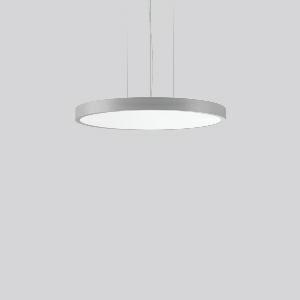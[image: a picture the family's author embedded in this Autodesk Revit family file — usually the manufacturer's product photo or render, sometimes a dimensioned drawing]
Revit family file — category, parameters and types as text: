
# Revit family: triona_round_p_312386_004_1_76_df9a
name_source: partatom
category: Lighting Fixtures
units: mm (PartAtom-declared; Revit-internal decimal feet)

## family parameters
Cut with Voids When Loaded = No
Host = Face
Light Source = No
Part Type = Normal
Room Calculation Point = No
Round Connector Dimension = Use Diameter
Shared = No

## types (1)
- TRIONA round P (1 x LED Modul 840, 9650 lm, 4000)
    Apparent Load = 106 VA
    CIE Flux Codes = 49 80 96 72 100
    Color Rendering = 80
    Color Temperature = 4000
    Default Elevation = 1800 mm
    Description = Series: TRIONA round
Decorative round LED pendant-mounted surface luminaire. Flat, seamless frame: aluminium extrusion profile, powder coated. Cover made of sheet steel, powder-coated. Canopy made of aluminium, powder-coated. Direct light emission through a diffuser plastic opal. Indirect light emission through a flush diffuser made of satin-finish plastic. Lightguide and diffuser made of non-yellowing plastic (PMMA). Lateral light emission (RZB SIDELITE technology) for above-average homogeneous light distribution. Direct 70%, indirect 30% light emission. 3-point steel cable suspension, steplessly adjustable. Easy installation with transparent, adjustable pendant cable and canopy with magnetic fixing. Driver integrated. 
Colour: silver, matt (approx. RAL 9006)
Diameter: 681 mm
Height: 52 mm
Suspension length: 500-1200 mm
Lamp: LED
Socket: without socket
Colour temperature: 4000K
Colour rendering index (CRI): 80
System power: 106 W
Rated luminous flux: 9650 lm
Luminous efficiency: 91 lm/W
Control gear: Converter, dimmable, DALI
Protection class: I
Type of protection: IP 20
    Height = 52 mm  [stored 0.170604 ft]
    Lamp = 1 x LED Modul 840
    Lamp Light Flux = 9650 lm
    Lamp count = 1
    Length = 681 mm
    Lifetime = 50000 h
    Luminous efficacy = 91 lm/W
    Manufacturer = RZB
    ModVariant = No
    Model = 312386.004.1.76
    Mounting Place = Ceiling
    Mounting Type = Pendant
    Number of Poles = 1
    OnlyDefault = Yes
    Power Factor = 1
    Product Name = TRIONA round P
    Product group = Pendant modular luminaires
    ProductGroupID = 906
    Protection Class = Protection class I
    Protection Degree = IP 20
    RLX_Detail_Level = 1
    RLX_Emergency_Light_Flux = 0 lm
    RLX_Emergency_Type = 0
    RLX_Emergency_Type_DB = No
    RlxData = <blob elided: 38017 chars, md5=f3ef890b>
    Socket = socket
    Standby Power = 0 W
    System Light Flux = 9650 lm
    System Power = 106 W
    Type Comments = Product without accessories
    Type Image = 312386.004.jpg
    URL = http://relux.com
    VarID = ---
    Voltage = 230 V
    Voltage Range = 220-240 V
    Weight = 0.00 kg
    Width = 0 mm  [stored 0 ft]

note: [stored X ft] marks values corroborated as IEEE doubles in the binary element streams (Revit-internal decimal feet)

## geometry (parser evidence)
native form markers: Blend x4, Sweep x10
no freeform markers — native parametric forms only
